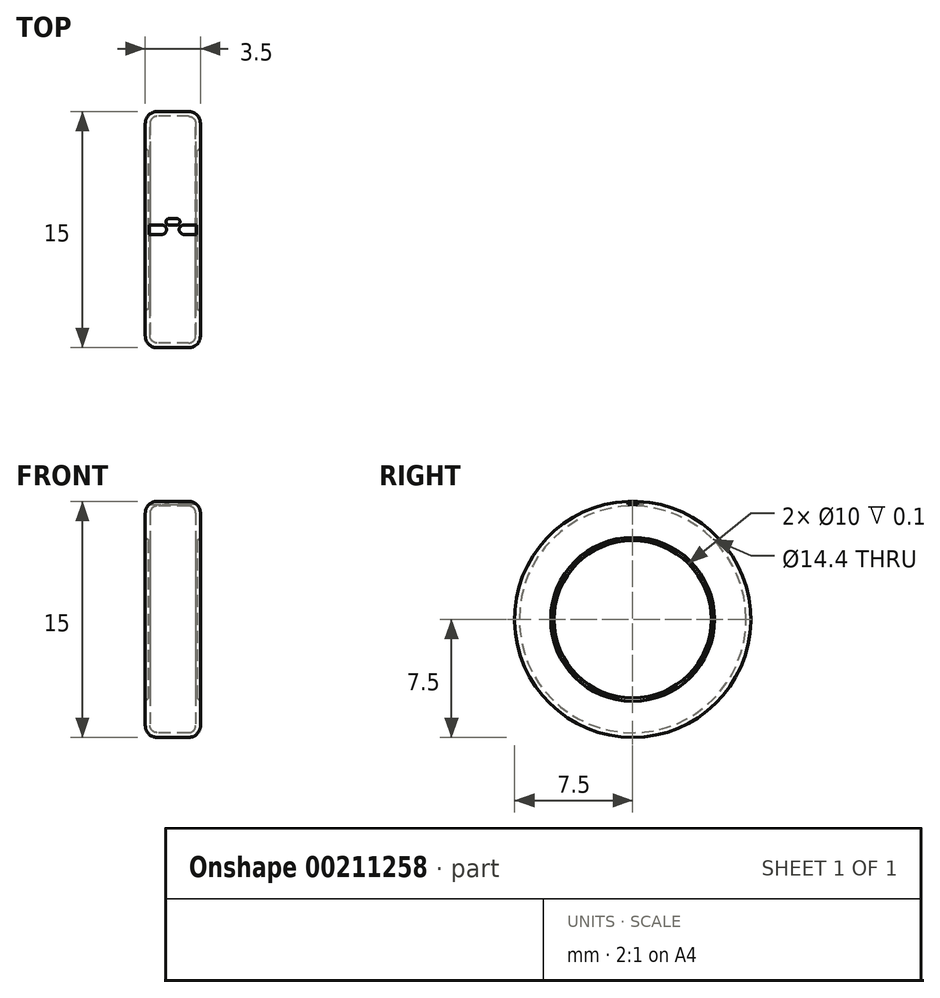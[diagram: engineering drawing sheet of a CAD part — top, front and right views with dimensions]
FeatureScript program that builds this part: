
annotation { "Feature Type Name" : "Feature", "Feature Type Description" : "" }
export const myFeature = defineFeature(function(context is Context, id is Id, definition is map)
    precondition{}
    {
        {
            var Q0;
            Q0=qCreatedBy(makeId("Front.planeOp"),FACE);
            var sketch = newSketch(context, id + "F0", { "sketchPlane" : qUnion([Q0])});
            skLineSegment(sketch, "E0", {"start": v(-29.59, 0) * mm, "end": v(30.89, 0) * mm, "construction": true});
            skLineSegment(sketch, "E1", {"start": v(0, 29.21) * mm, "end": v(0, -29.1) * mm, "construction": true});
            skLineSegment(sketch, "E2", {"start": v(0, -7.5) * mm, "end": v(-1, -7.5) * mm});
            skLineSegment(sketch, "E3", {"start": v(-1.75, -6.75) * mm, "end": v(-1.75, -5) * mm});
            skLineSegment(sketch, "E4", {"start": v(-1.75, -5) * mm, "end": v(-1.45, -5) * mm});
            skLineSegment(sketch, "E5", {"start": v(-1.45, -5) * mm, "end": v(-1.45, -6.75) * mm});
            skLineSegment(sketch, "E6", {"start": v(-1, -7.2) * mm, "end": v(0, -7.2) * mm});
            skPoint(sketch, "E7.visualSharp", {"position": v(-1.75, -7.5) * mm});
            skArc(sketch, "E7.filletArc", {"start": v(-1.75, -6.75) * mm, "mid": v(-1.53, -7.28) * mm, "end": v(-1, -7.5) * mm});
            skPoint(sketch, "E8.visualSharp", {"position": v(-1.45, -7.2) * mm});
            skArc(sketch, "E8.filletArc", {"start": v(-1.45, -6.75) * mm, "mid": v(-1.32, -7.07) * mm, "end": v(-1, -7.2) * mm});
            skLineSegment(sketch, "E9.MirrorCS", {"start": v(1.75, -5) * mm, "end": v(1.45, -5) * mm});
            skArc(sketch, "E10.MirrorCS", {"start": v(1.45, -6.75) * mm, "mid": v(1.32, -7.07) * mm, "end": v(1, -7.2) * mm});
            skArc(sketch, "E11.MirrorCS", {"start": v(1.75, -6.75) * mm, "mid": v(1.53, -7.28) * mm, "end": v(1, -7.5) * mm});
            skLineSegment(sketch, "E12.MirrorCS", {"start": v(1.45, -5) * mm, "end": v(1.45, -6.75) * mm});
            skPoint(sketch, "E13.MirrorP", {"position": v(1.75, -7.5) * mm});
            skLineSegment(sketch, "E14.MirrorCS", {"start": v(1.75, -6.75) * mm, "end": v(1.75, -5) * mm});
            skPoint(sketch, "E15.MirrorP", {"position": v(1.45, -7.2) * mm});
            skLineSegment(sketch, "E16.MirrorCS", {"start": v(1, -7.2) * mm, "end": v(0, -7.2) * mm});
            skLineSegment(sketch, "E17.MirrorCS", {"start": v(0, -7.5) * mm, "end": v(1, -7.5) * mm});
            skSolve(sketch);
        }
        {
            var Q0;
            Q0=qSketchRegion(id+"F0",true);
            var Q1;
            Q1=sQuery(id+"F0.wireOp",EDGE,"E0");
            revolve(context, id + "F1", {"entities" : qUnion([Q0]), "axis" : qUnion([Q1]), "revolveType" : RevolveType.FULL});
        }
        {
            var Q0;
            Q0=qCreatedBy(makeId("Top.planeOp"),FACE);
            cPlane(context, id + "F2", {"entities" : qUnion([Q0]), "cplaneType" : CPlaneType.OFFSET, "offset" : 7.5 * mm, "width" : 150 * mm, "height" : 150 * mm});
        }
        {
            var Q0;
            Q0=qCreatedBy(id+"F2.planeOp",FACE);
            var sketch = newSketch(context, id + "F3", { "sketchPlane" : qUnion([Q0])});
            skLineSegment(sketch, "E18", {"start": v(-0.25, 0.5) * mm, "end": v(0.25, 0.5) * mm});
            skArc(sketch, "E19.0.startCap", {"start": v(-0.25, 0.3) * mm, "mid": v(-0.45, 0.5) * mm, "end": v(-0.25, 0.7) * mm});
            skArc(sketch, "E19.0.endCap", {"start": v(0.25, 0.7) * mm, "mid": v(0.45, 0.5) * mm, "end": v(0.25, 0.3) * mm});
            skLineSegment(sketch, "E19.0.left", {"start": v(-0.25, 0.7) * mm, "end": v(0.25, 0.7) * mm});
            skLineSegment(sketch, "E19.0.right", {"start": v(-0.25, 0.3) * mm, "end": v(0.25, 0.3) * mm});
            skLineSegment(sketch, "E20", {"start": v(0, 0) * mm, "end": v(0, 0.5) * mm, "construction": true});
            skArc(sketch, "E21", {"start": v(-0.7, -0.3) * mm, "mid": v(-0.4, 0) * mm, "end": v(-0.7, 0.3) * mm});
            skLineSegment(sketch, "E22", {"start": v(-0.7, 0.3) * mm, "end": v(-1.7, 0.3) * mm});
            skLineSegment(sketch, "E23", {"start": v(-1.7, 0.3) * mm, "end": v(-1.7, -0.3) * mm});
            skLineSegment(sketch, "E24", {"start": v(-1.7, -0.3) * mm, "end": v(-0.7, -0.3) * mm});
            skLineSegment(sketch, "E25.MirrorCS", {"start": v(1.7, -0.3) * mm, "end": v(0.7, -0.3) * mm});
            skLineSegment(sketch, "E26.MirrorCS", {"start": v(1.7, 0.3) * mm, "end": v(1.7, -0.3) * mm});
            skLineSegment(sketch, "E27.MirrorCS", {"start": v(0.7, 0.3) * mm, "end": v(1.7, 0.3) * mm});
            skArc(sketch, "E28.MirrorCS", {"start": v(0.7, -0.3) * mm, "mid": v(0.4, 0) * mm, "end": v(0.7, 0.3) * mm});
            skSolve(sketch);
        }
        {
            var Q0;
            Q0=qSketchRegion(id+"F3",true);
            extrude(context, id + "F4", {"entities" : qUnion([Q0]), "operationType" : NewBodyOperationType.REMOVE, "oppositeDirection" : true, "depth" : .2 * mm});
        }
        {
            var Q0;
            Q0=makeQuery(id+"F1.opRevolve","SWEPT_EDGE",EDGE,{"disambiguationData":[OSD([sQuery(id+"F0.wireOp",EDGE,"E3"),sQuery(id+"F0.wireOp",EDGE,"E4")])]});
            var Q1;
            Q1=makeQuery(id+"F1.opRevolve","SWEPT_EDGE",EDGE,{"disambiguationData":[OSD([sQuery(id+"F0.wireOp",EDGE,"E9.MirrorCS"),sQuery(id+"F0.wireOp",EDGE,"E14.MirrorCS")])]});
            chamfer(context, id + "F5", {"entities" : qUnion([Q0, Q1]), "width" : .2 * mm, "tangentPropagation" : true});
        }
    });
